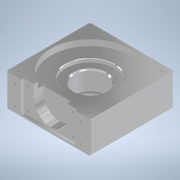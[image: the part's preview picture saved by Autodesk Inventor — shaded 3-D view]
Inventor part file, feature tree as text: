
AUTODESK INVENTOR PART (.ipt)
format: ipt  version: 2022.1 (Build 261234000, 234)  size: 322,048 bytes
history: native  units: mm
features: sketch x9, extrude x6, other x6, hole x5, projected_geometry x4, chamfer x3, fillet x3, reference x3
ambient origin geometry x8: Origin, YZ Plane, XZ Plane, XY Plane, X Axis, Y Axis, Z Axis, Center Point
bodies: Solid1 (feature_tree)
feature tree (39):
  sketch  "Sketch1"  dims[d0=130.0mm d1=140.0mm]
  extrude  "Extrusion1"  Depth=140.0mm
  extrude  "Extrusion2"  Depth=10.0mm TaperAngle=0.0deg
  extrude  "Extrusion3"  Depth=45.0mm
  other  "Plate Mounting Holes"
  other  "PlateHole"
  extrude  "Extrusion4"  Depth=5.0mm
  extrude  "Extrusion5"  Depth=5.0mm
  chamfer  "Chamfer2"  Distance=6.0mm
  chamfer  "Chamfer3"  Distance=20.0mm
  hole  "Hole2"  [1 undecoded]
  extrude  "Extrusion6"  Depth=2.0mm TaperAngle=45.0deg
  fillet  "Fillet1"  Radius=4.0mm
  hole  "Hole3"  [1 undecoded]
  chamfer  "Chamfer5"  Distance=30.0mm
  hole  "Hole4"  [1 undecoded]
  fillet  "Fillet2"  Radius=4.0mm
  hole  "Hole5"  [1 undecoded]
  hole  "Hole6"  [1 undecoded]
  fillet  "Fillet3"  Radius=32.0mm
  sketch  "Sketch2"  dims[d2=140.0mm d4=10.0mm d5=0.0mm]
  projected_geometry  "Projected Loop5"
  sketch  "Sketch7"  dims[d6=45.0mm d7=0.0mm d8=52.0mm]
  projected_geometry  "Projected Loop6"
  sketch  "Sketch10"  dims[d9=38.0mm d10=0.0mm d14=5.0mm]
  reference  "Reference8"
  sketch  "Sketch11"  dims[d15=5.0mm d16=80.0mm]
  projected_geometry  "Projected Loop7"
  sketch  "Sketch13"  dims[d18=5.0mm]
  sketch  "Sketch14"  dims[d19=80.0mm d20=6.0mm d21=0.0mm d22=20.0mm d23=0.0mm]
  reference  "Reference13"
  sketch  "Sketch15"  dims[d24=20.0mm d25=56.0mm]
  sketch  "Sketch16"  dims[d26=2.0mm d27=2.0mm d28=45.0deg d29=1.0mm d30=2.0mm d31=45.0deg d39=3.242mm d40=8.0mm d41=4.0mm d42=2.0mm d43=90.0deg d44=11.8mm d45=20.594885mm d47=4.0mm d48=0.0mm d49=2.0mm d50=30.0mm d51=90.0mm d55=3.242mm d56=8.0mm d57=8.0mm d58=4.6mm d59=90.0deg d60=11.8mm d61=20.594885mm d62=4.0mm d63=2.0mm d64=45.0deg d65=2.459mm d66=6.0mm d67=6.5mm d68=3.4mm d69=90.0deg d70=8.8mm d71=20.594885mm d72=3.0mm d73=110.0mm d74=32.0mm d75=3.242mm d76=8.0mm d77=4.0mm d78=2.0mm d79=90.0deg d80=11.8mm d81=20.594885mm d82=3.242mm d83=8.0mm d84=4.0mm d85=2.0mm d86=90.0deg d87=11.8mm d88=20.594885mm d89=3.0mm d32=0.5mm d33=0.872665mm d34=0.5mm d35=0.872665mm d46=0.5mm]
  projected_geometry  "Projected Loop9"
  reference  "Reference18"
  other  "SistemaElevacionV2.iam"
  other  "SeguroRodamientos:1"
  other  "Cubierta de soporte base:1"
  other  "Montura de motor de elevación:1"
note: 5 required parameter values undecoded (feature->parameter linkage not recoverable at this tier; creation-order binding heuristic only, values carry confidence <= 0.55)
